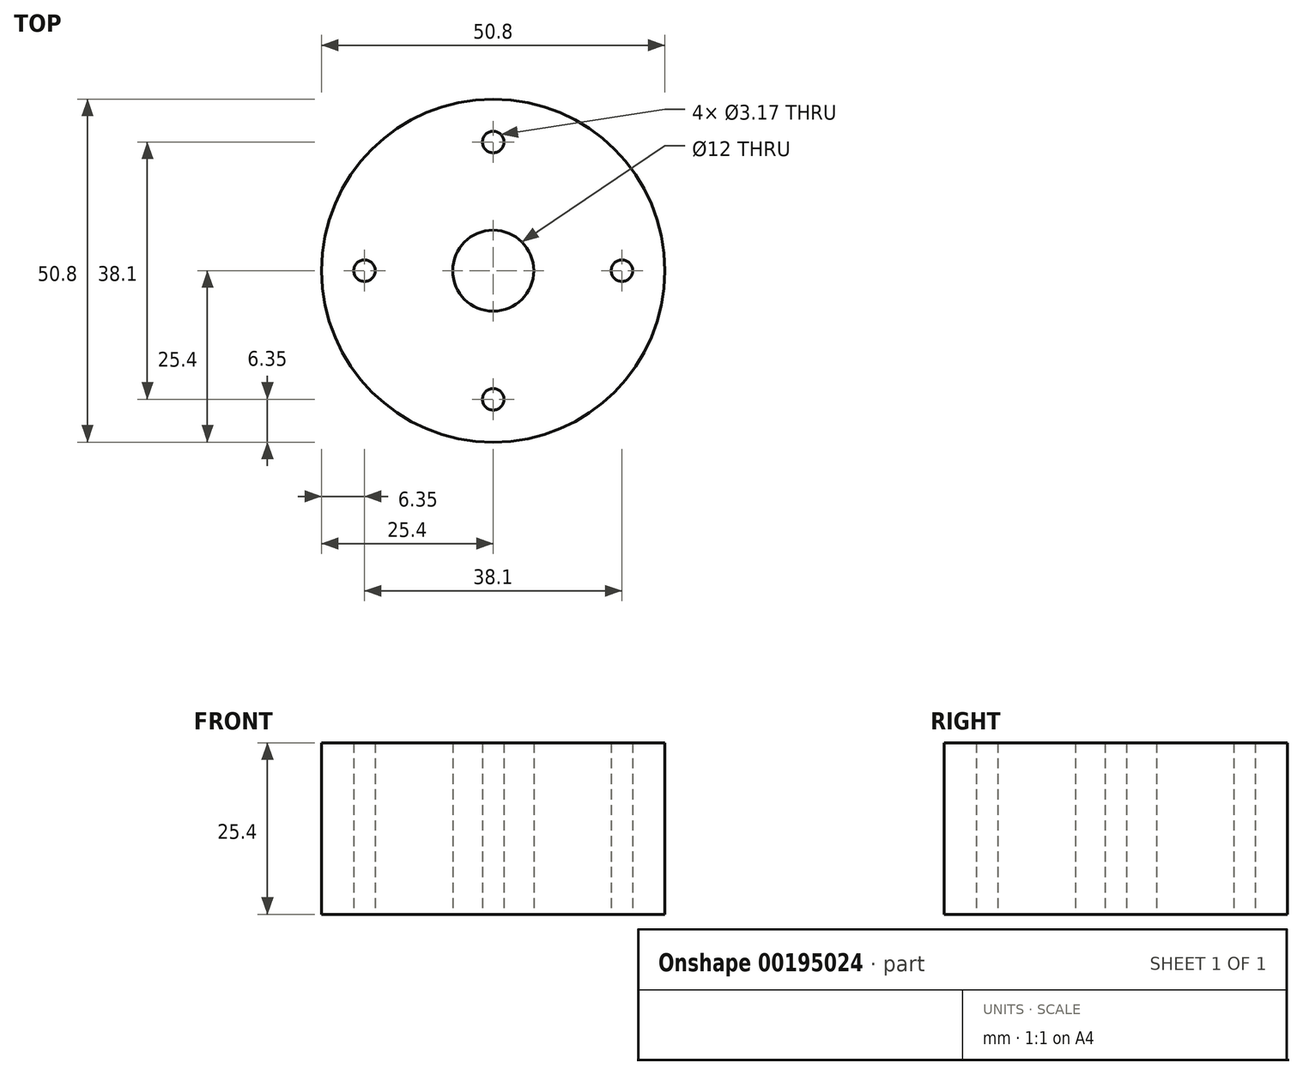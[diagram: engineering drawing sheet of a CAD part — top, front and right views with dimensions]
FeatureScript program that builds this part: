
annotation { "Feature Type Name" : "Feature", "Feature Type Description" : "" }
export const myFeature = defineFeature(function(context is Context, id is Id, definition is map)
    precondition{}
    {
        {
            var Q0;
            Q0=qCreatedBy(makeId("Top.planeOp"),FACE);
            var sketch = newSketch(context, id + "F0", { "sketchPlane" : qUnion([Q0])});
            skCircle(sketch, "E0", {"center": v(0, 0) * mm, "radius": 25.4 * mm});
            skCircle(sketch, "E1", {"center": v(0, 0) * mm, "radius": 6 * mm});
            skCircle(sketch, "E2", {"center": v(0, 0) * mm, "radius": 19.05 * mm, "construction": true});
            skCircle(sketch, "E3", {"center": v(0, 19.05) * mm, "radius": 1.59 * mm});
            skCircle(sketch, "E4.1.0", {"center": v(-19.05, 0) * mm, "radius": 1.59 * mm});
            skCircle(sketch, "E4.2.0", {"center": v(0, -19.05) * mm, "radius": 1.59 * mm});
            skCircle(sketch, "E4.3.0", {"center": v(19.05, 0) * mm, "radius": 1.59 * mm});
            skSolve(sketch);
        }
        {
            var Q0;
            Q0 = qSketchRegion(id + "F0", true);
            extrude(context, id + "F1", {"entities" : qUnion([Q0]), "depth" : 19.05 * mm});
        }
        {
            var Q0;
            Q0 = qSketchRegion(id + "F0", true);
            extrude(context, id + "F2", {"entities" : qUnion([Q0]), "operationType" : NewBodyOperationType.ADD, "depth" : 25.4 * mm});
        }
    });
